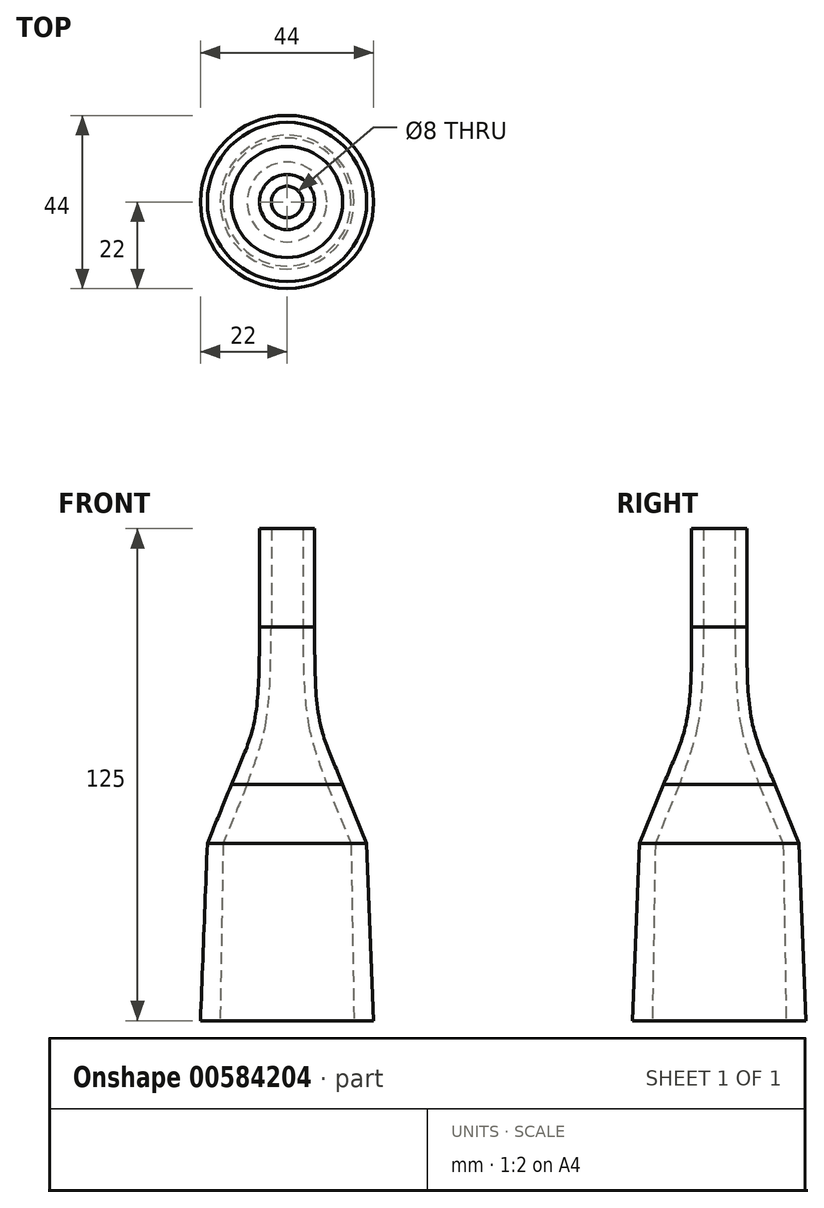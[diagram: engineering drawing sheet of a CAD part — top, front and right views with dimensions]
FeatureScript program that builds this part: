
annotation { "Feature Type Name" : "Feature", "Feature Type Description" : "" }
export const myFeature = defineFeature(function(context is Context, id is Id, definition is map)
    precondition{}
    {
        {
            var Q0;
            Q0=qCreatedBy(makeId("Front.planeOp"),FACE);
            var sketch = newSketch(context, id + "F0", { "sketchPlane" : qUnion([Q0])});
            skLineSegment(sketch, "E0", {"start": v(0, 0) * mm, "end": v(0, 45) * mm});
            skLineSegment(sketch, "E1", {"start": v(0, 45) * mm, "end": v(-16.25, 45) * mm});
            skLineSegment(sketch, "E2", {"start": v(0, 45) * mm, "end": v(16.25, 45) * mm});
            skLineSegment(sketch, "E3", {"start": v(-16.25, 45) * mm, "end": v(-20.25, 45) * mm});
            skLineSegment(sketch, "E4", {"start": v(16.25, 45) * mm, "end": v(20.25, 45) * mm});
            skLineSegment(sketch, "E5", {"start": v(0, 45) * mm, "end": v(0, 75) * mm});
            skLineSegment(sketch, "E6", {"start": v(0, 75) * mm, "end": v(4, 75) * mm});
            skLineSegment(sketch, "E7", {"start": v(10.12, 60) * mm, "end": v(16.25, 45) * mm});
            skLineSegment(sketch, "E8", {"start": v(-10.12, 60) * mm, "end": v(-16.25, 45) * mm});
            skLineSegment(sketch, "E9", {"start": v(-4, 75) * mm, "end": v(-5.5, 75) * mm});
            skLineSegment(sketch, "E10", {"start": v(-14.12, 60) * mm, "end": v(-20.25, 45) * mm});
            skLineSegment(sketch, "E11", {"start": v(14.12, 60) * mm, "end": v(20.25, 45) * mm});
            skLineSegment(sketch, "E12.top", {"start": v(-4, 125) * mm, "end": v(-7, 125) * mm});
            skLineSegment(sketch, "E12.left", {"start": v(-4, 100) * mm, "end": v(-4, 125) * mm});
            skLineSegment(sketch, "E12.right", {"start": v(-7, 100) * mm, "end": v(-7, 125) * mm});
            skLineSegment(sketch, "E13.bottom", {"start": v(4, 75) * mm, "end": v(5.5, 75) * mm});
            skLineSegment(sketch, "E13.top", {"start": v(4, 125) * mm, "end": v(7, 125) * mm});
            skLineSegment(sketch, "E13.left", {"start": v(4, 100) * mm, "end": v(4, 125) * mm});
            skLineSegment(sketch, "E13.right", {"start": v(7, 100) * mm, "end": v(7, 125) * mm});
            skLineSegment(sketch, "E14", {"start": v(-4, 125) * mm, "end": v(4, 125) * mm});
            skLineSegment(sketch, "E15", {"start": v(0, 75) * mm, "end": v(0, 125) * mm});
            skLineSegment(sketch, "E16", {"start": v(0, 0) * mm, "end": v(17, 0) * mm});
            skLineSegment(sketch, "E17", {"start": v(0, 0) * mm, "end": v(-17, 0) * mm});
            skLineSegment(sketch, "E18", {"start": v(17, 0) * mm, "end": v(22, 0) * mm});
            skLineSegment(sketch, "E19", {"start": v(-17, 0) * mm, "end": v(-22, 0) * mm});
            skLineSegment(sketch, "E20", {"start": v(-16.25, 45) * mm, "end": v(-17, 0) * mm});
            skLineSegment(sketch, "E21", {"start": v(16.25, 45) * mm, "end": v(17, 0) * mm});
            skLineSegment(sketch, "E22", {"start": v(20.25, 45) * mm, "end": v(22, 0) * mm});
            skLineSegment(sketch, "E23", {"start": v(-20.25, 45) * mm, "end": v(-22, 0) * mm});
            skLineSegment(sketch, "E24", {"start": v(-4, 75) * mm, "end": v(0, 75) * mm});
            skFitSpline(sketch, "E25", {"points": [v(-10.12, 60) * mm, v(-5.5, 75) * mm, v(-4, 100) * mm], "startDerivative": vector(10.83, 31.68) * mm, "endDerivative": vector(0.82, 47.69) * mm});
            skFitSpline(sketch, "E26", {"points": [v(14.12, 60) * mm, v(8.5, 75) * mm, v(7, 100) * mm], "startDerivative": vector(-7.65, 31.97) * mm, "endDerivative": vector(-4.72, 47.4) * mm});
            skFitSpline(sketch, "E27", {"points": [v(10.12, 60) * mm, v(5.5, 75) * mm, v(4, 100) * mm], "startDerivative": vector(-10.83, 31.68) * mm, "endDerivative": vector(-0.82, 47.69) * mm});
            skLineSegment(sketch, "E28", {"start": v(-8.5, 75.14) * mm, "end": v(-5.5, 75) * mm});
            skFitSpline(sketch, "E29", {"points": [v(-14.12, 60) * mm, v(-8.5, 75.14) * mm, v(-7, 100) * mm], "startDerivative": vector(12.15, 31.78) * mm, "endDerivative": vector(0.54, 47.62) * mm});
            skSolve(sketch);
        }
        {
            var Q0;
            Q0=makeQuery(id+"F0.imprint","IMPRINT",FACE,{"disambiguationData":[TD([[makeQuery(id+"F0.imprint","IMPRINT",EDGE,{"derivedFrom":sQuery(id+"F0.wireOp",EDGE,"E3")}),1.0]])]});
            var Q1;
            Q1=sQuery(id+"F0.wireOp",EDGE,"E0");
            revolve(context, id + "F1", {"entities" : qUnion([Q0]), "axis" : qUnion([Q1]), "revolveType" : RevolveType.FULL});
        }
        {
            var Q0;
            Q0=makeQuery(id+"F0.imprint","IMPRINT",FACE,{"disambiguationData":[TD([[makeQuery(id+"F0.imprint","IMPRINT",EDGE,{"derivedFrom":sQuery(id+"F0.wireOp",EDGE,"E3")}),-1.0]])]});
            var Q1;
            Q1=sQuery(id+"F0.wireOp",EDGE,"E5");
            revolve(context, id + "F2", {"operationType" : NewBodyOperationType.ADD, "entities" : qUnion([Q0]), "axis" : qUnion([Q1]), "revolveType" : RevolveType.FULL});
        }
        {
            var Q0;
            Q0=makeQuery(id+"F0.imprint","IMPRINT",FACE,{"disambiguationData":[TD([[makeQuery(id+"F0.imprint","IMPRINT",EDGE,{"derivedFrom":sQuery(id+"F0.wireOp",EDGE,"E12.top")}),1.0]])]});
            var Q1;
            Q1=sQuery(id+"F0.wireOp",EDGE,"E15");
            revolve(context, id + "F3", {"operationType" : NewBodyOperationType.ADD, "entities" : qUnion([Q0]), "axis" : qUnion([Q1]), "revolveType" : RevolveType.FULL});
        }
    });
